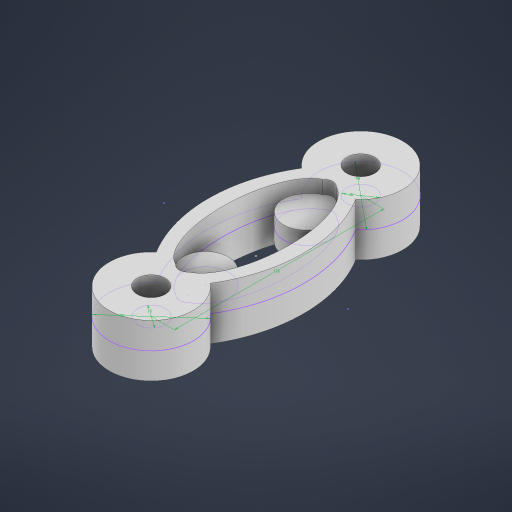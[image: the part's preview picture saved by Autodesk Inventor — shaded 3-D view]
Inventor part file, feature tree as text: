
AUTODESK INVENTOR PART (.ipt)
format: ipt  version: 2024.3 (Build 283343000, 343)  size: 235,008 bytes
history: native  units: mm
features: extrude x2, sketch x1
ambient origin geometry x8: Origin, YZ Plane, XZ Plane, XY Plane, X Axis, Y Axis, Z Axis, Center Point
bodies: Body1 (feature_tree)
feature tree (3):
  sketch  "Sketch1"  dims[d0=16.0mm d1=16.0mm d2=120.0mm d4=48.0mm d5=48.0mm d20=30.0mm d21=0.0mm d22=15.0mm d23=0.0mm]
  extrude  "Extrusion2"  Depth=15.0mm
  extrude  "Extrusion3"  Depth=15.0mm
